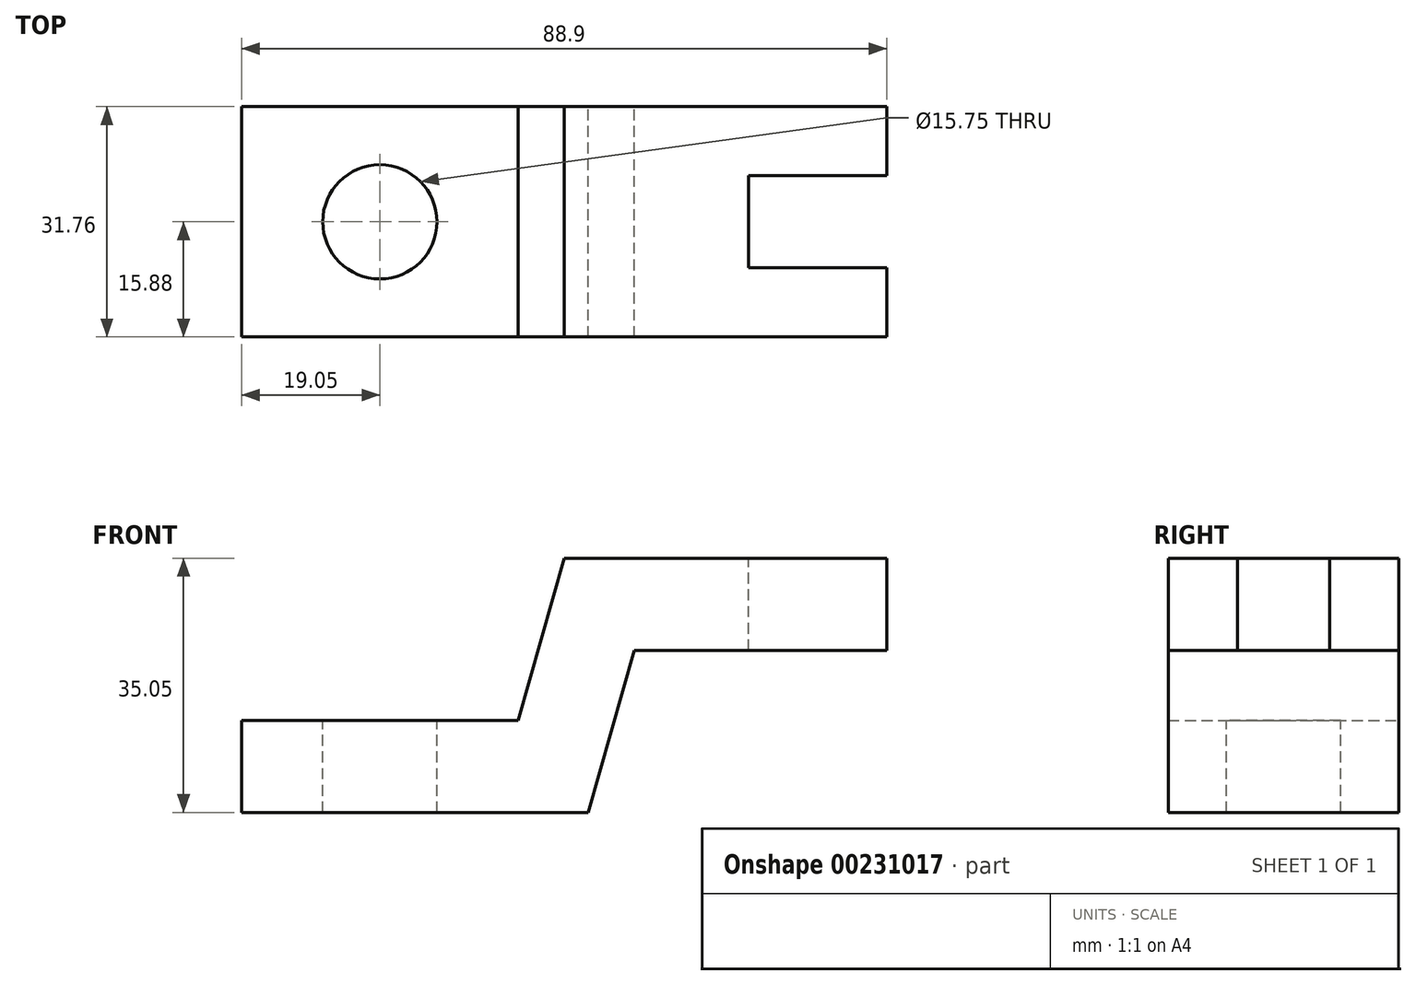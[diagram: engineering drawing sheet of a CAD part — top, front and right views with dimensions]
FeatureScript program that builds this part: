
annotation { "Feature Type Name" : "Feature", "Feature Type Description" : "" }
export const myFeature = defineFeature(function(context is Context, id is Id, definition is map)
    precondition{}
    {
        {
            var Q0;
            Q0=qCreatedBy(makeId("Front.planeOp"),FACE);
            var sketch = newSketch(context, id + "F0", { "sketchPlane" : qUnion([Q0])});
            skLineSegment(sketch, "E0", {"start": v(0, 0) * mm, "end": v(38.1, 0) * mm});
            skLineSegment(sketch, "E1", {"start": v(0, 0) * mm, "end": v(0, 12.7) * mm});
            skLineSegment(sketch, "E2", {"start": v(0, 12.7) * mm, "end": v(38.1, 12.7) * mm});
            skLineSegment(sketch, "E3", {"start": v(38.1, 0) * mm, "end": v(47.75, 0) * mm});
            skLineSegment(sketch, "E4", {"start": v(88.9, 22.35) * mm, "end": v(54.1, 22.35) * mm});
            skLineSegment(sketch, "E5", {"start": v(54.1, 22.35) * mm, "end": v(47.75, 0) * mm});
            skLineSegment(sketch, "E6", {"start": v(88.9, 22.35) * mm, "end": v(88.9, 35.05) * mm});
            skLineSegment(sketch, "E7", {"start": v(88.9, 35.05) * mm, "end": v(44.45, 35.05) * mm});
            skLineSegment(sketch, "E8", {"start": v(44.45, 35.05) * mm, "end": v(38.1, 12.7) * mm});
            skSolve(sketch);
        }
        {
            var Q0;
            Q0 = qSketchRegion(id + "F0", true);
            extrude(context, id + "F1", {"entities" : qUnion([Q0]), "endBound" : BoundingType.SYMMETRIC, "depth" : 31.75 * mm});
        }
        {
            var Q0;
            Q0=makeQuery(id+"F1.opExtrude","SWEPT_FACE",FACE,{"disambiguationData":[OSD([sQuery(id+"F0.wireOp",EDGE,"E2")])]});
            var sketch = newSketch(context, id + "F2", { "sketchPlane" : qUnion([Q0])});
            skCircle(sketch, "E9", {"center": v(19.05, 0) * mm, "radius": 7.87 * mm});
            skSolve(sketch);
        }
        {
            var Q0;
            Q0=makeQuery(id+"F2.imprint","IMPRINT",FACE,{"disambiguationData":[TD([[makeQuery(id+"F2.imprint","IMPRINT",EDGE,{"derivedFrom":sQuery(id+"F2.wireOp",EDGE,"E9")}),1.0]])]});
            extrude(context, id + "F3", {"entities" : qUnion([Q0]), "operationType" : NewBodyOperationType.REMOVE, "endBound" : BoundingType.THROUGH_ALL, "oppositeDirection" : true, "depth" : 25.4 * mm});
        }
        {
            var Q0;
            Q0=makeQuery(id+"F1.opExtrude","SWEPT_FACE",FACE,{"disambiguationData":[OSD([sQuery(id+"F0.wireOp",EDGE,"E7")])]});
            var sketch = newSketch(context, id + "F4", { "sketchPlane" : qUnion([Q0])});
            skLineSegment(sketch, "E10", {"start": v(88.9, -6.35) * mm, "end": v(69.85, -6.35) * mm});
            skLineSegment(sketch, "E11", {"start": v(69.85, -6.35) * mm, "end": v(69.85, 0) * mm});
            skLineSegment(sketch, "E12", {"start": v(69.85, 0) * mm, "end": v(69.85, 6.35) * mm});
            skLineSegment(sketch, "E13", {"start": v(69.85, 6.35) * mm, "end": v(88.9, 6.35) * mm});
            skLineSegment(sketch, "E14", {"start": v(88.9, 6.35) * mm, "end": v(88.9, -6.35) * mm});
            skSolve(sketch);
        }
        {
            var Q0;
            Q0=makeQuery(id+"F4.imprint","IMPRINT",FACE,{"disambiguationData":[TD([[makeQuery(id+"F4.imprint","IMPRINT",EDGE,{"derivedFrom":sQuery(id+"F4.wireOp",EDGE,"E10")}),-1.0]])]});
            extrude(context, id + "F5", {"entities" : qUnion([Q0]), "operationType" : NewBodyOperationType.REMOVE, "endBound" : BoundingType.THROUGH_ALL, "oppositeDirection" : true, "depth" : 25.4 * mm});
        }
    });
